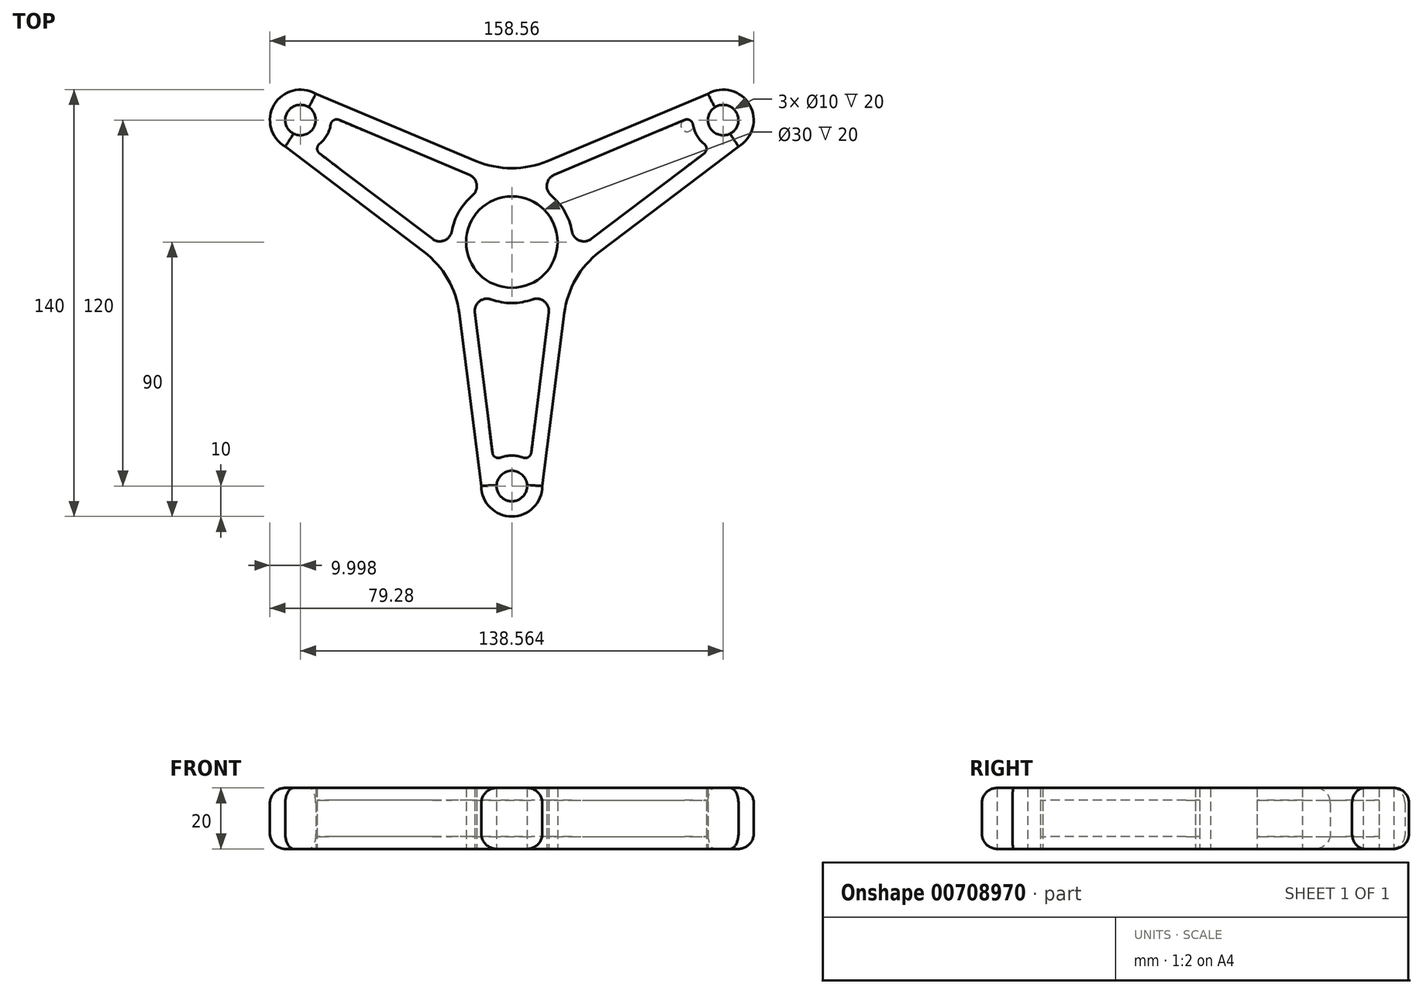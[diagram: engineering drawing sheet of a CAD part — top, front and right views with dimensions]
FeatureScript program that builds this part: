
annotation { "Feature Type Name" : "Feature", "Feature Type Description" : "" }
export const myFeature = defineFeature(function(context is Context, id is Id, definition is map)
    precondition{}
    {
        {
            var Q0;
            Q0=qCreatedBy(makeId("Top.planeOp"),FACE);
            var sketch = newSketch(context, id + "F0", { "sketchPlane" : qUnion([Q0])});
            skCircle(sketch, "E0", {"center": v(0, 0) * mm, "radius": 15 * mm});
            skLineSegment(sketch, "E1", {"start": v(0, 0) * mm, "end": v(-87.42, 50.47) * mm, "construction": true});
            skLineSegment(sketch, "E2", {"start": v(0, 0) * mm, "end": v(80.4, 46.42) * mm, "construction": true});
            skCircle(sketch, "E3", {"center": v(0, -80) * mm, "radius": 5 * mm});
            skLineSegment(sketch, "E4", {"start": v(0, 0) * mm, "end": v(0, -98.48) * mm, "construction": true});
            skArc(sketch, "E5", {"start": v(-10, -80) * mm, "mid": v(0, -90) * mm, "end": v(10, -80) * mm});
            skLineSegment(sketch, "E6", {"start": v(15, 0) * mm, "end": v(14.54, -3.7) * mm});
            skLineSegment(sketch, "E7", {"start": v(-15, 0) * mm, "end": v(-14.54, -3.7) * mm});
            skPoint(sketch, "E8.orphan", {"position": v(-5, -80) * mm});
            skPoint(sketch, "E9.orphan", {"position": v(5, -80) * mm});
            skArc(sketch, "E10.trimOffspring", {"start": v(3.65, -70.7) * mm, "mid": v(0, -70) * mm, "end": v(-3.65, -70.7) * mm});
            skArc(sketch, "E11.filletArc", {"start": v(-6.37, -69.08) * mm, "mid": v(-5.4, -70.55) * mm, "end": v(-3.65, -70.7) * mm});
            skArc(sketch, "E12.filletArc", {"start": v(3.65, -70.7) * mm, "mid": v(5.4, -70.55) * mm, "end": v(6.37, -69.08) * mm});
            skLineSegment(sketch, "E13.trimOffspring", {"start": v(-6.83, -65.35) * mm, "end": v(-6.37, -69.08) * mm});
            skLineSegment(sketch, "E14.trimOffspring", {"start": v(7.68, -58.58) * mm, "end": v(6.37, -69.08) * mm});
            skLineSegment(sketch, "E15", {"start": v(80.4, 46.42) * mm, "end": v(-61.57, -35.55) * mm, "construction": true});
            skLineSegment(sketch, "E16.trimOffspring", {"start": v(-17.2, -23.33) * mm, "end": v(-10, -80) * mm});
            skLineSegment(sketch, "E17", {"start": v(-87.42, 50.47) * mm, "end": v(59.57, -34.4) * mm, "construction": true});
            skLineSegment(sketch, "E18.trimOffspring", {"start": v(17.2, -23.33) * mm, "end": v(10, -80) * mm});
            skCircle(sketch, "E19", {"center": v(-69.28, 40) * mm, "radius": 5 * mm});
            skArc(sketch, "E20", {"start": v(-64.28, 48.66) * mm, "mid": v(-77.94, 45) * mm, "end": v(-74.28, 31.34) * mm});
            skLineSegment(sketch, "E21", {"start": v(-7.5, -13) * mm, "end": v(-10.47, -10.74) * mm});
            skLineSegment(sketch, "E22", {"start": v(7.5, 13) * mm, "end": v(4.07, 14.44) * mm});
            skPoint(sketch, "E23.orphan", {"position": v(-66.78, 44.33) * mm});
            skPoint(sketch, "E24.orphan", {"position": v(-71.78, 35.67) * mm});
            skArc(sketch, "E25.trimOffspring", {"start": v(-63.04, 32.18) * mm, "mid": v(-60.62, 35) * mm, "end": v(-59.4, 38.5) * mm});
            skArc(sketch, "E26.filletArc", {"start": v(-56.64, 40.05) * mm, "mid": v(-58.4, 39.95) * mm, "end": v(-59.4, 38.5) * mm});
            skArc(sketch, "E27.filletArc", {"start": v(-63.04, 32.18) * mm, "mid": v(-63.8, 30.6) * mm, "end": v(-63, 29.03) * mm});
            skLineSegment(sketch, "E28.trimOffspring", {"start": v(-13.92, 22.03) * mm, "end": v(-56.64, 40.05) * mm});
            skLineSegment(sketch, "E29.trimOffspring", {"start": v(-26.04, 1.04) * mm, "end": v(-63, 29.03) * mm});
            skArc(sketch, "E30.trimOffspring", {"start": v(-12.9, 15.29) * mm, "mid": v(-17.32, 10) * mm, "end": v(-19.69, 3.53) * mm});
            skArc(sketch, "E31.filletArc", {"start": v(-12.9, 15.29) * mm, "mid": v(-11.52, 18.94) * mm, "end": v(-13.92, 22.03) * mm});
            skArc(sketch, "E32.filletArc", {"start": v(-26.04, 1.04) * mm, "mid": v(-22.17, 0.5) * mm, "end": v(-19.69, 3.53) * mm});
            skArc(sketch, "E33", {"start": v(-6.79, -18.81) * mm, "mid": v(0, -20) * mm, "end": v(6.79, -18.81) * mm});
            skLineSegment(sketch, "E34.trimOffspring", {"start": v(-11.6, 26.56) * mm, "end": v(-64.28, 48.66) * mm});
            skLineSegment(sketch, "E35.trimOffspring", {"start": v(-28.8, -3.23) * mm, "end": v(-74.28, 31.34) * mm});
            skLineSegment(sketch, "E36.0", {"start": v(-64.28, 48.66) * mm, "end": v(-74.28, 31.34) * mm, "construction": true});
            skArc(sketch, "E37.filletArc", {"start": v(-17.2, -23.33) * mm, "mid": v(-20.98, -12.11) * mm, "end": v(-28.8, -3.23) * mm});
            skLineSegment(sketch, "E38.trimOffspring", {"start": v(-12.12, -23.07) * mm, "end": v(-6.83, -65.35) * mm});
            skLineSegment(sketch, "E39.trimOffspring", {"start": v(12.12, -23.07) * mm, "end": v(6.37, -69.08) * mm});
            skArc(sketch, "E40.trimOffspring", {"start": v(17.32, 10) * mm, "mid": v(15.34, 12.83) * mm, "end": v(12.9, 15.29) * mm});
            skArc(sketch, "E41.filletArc", {"start": v(12.12, -23.07) * mm, "mid": v(10.64, -19.45) * mm, "end": v(6.79, -18.81) * mm});
            skArc(sketch, "E42.filletArc", {"start": v(-6.79, -18.81) * mm, "mid": v(-10.64, -19.45) * mm, "end": v(-12.12, -23.07) * mm});
            skLineSegment(sketch, "E43", {"start": v(0, 0) * mm, "end": v(0, -100.94) * mm, "construction": true});
            skLineSegment(sketch, "E44", {"start": v(0, 0) * mm, "end": v(-80.4, 46.42) * mm, "construction": true});
            skCircle(sketch, "E45", {"center": v(69.28, 40) * mm, "radius": 5 * mm});
            skLineSegment(sketch, "E46", {"start": v(0, 0) * mm, "end": v(85.28, 49.24) * mm, "construction": true});
            skArc(sketch, "E47", {"start": v(74.28, 31.34) * mm, "mid": v(77.94, 45) * mm, "end": v(64.28, 48.66) * mm});
            skLineSegment(sketch, "E48", {"start": v(-7.5, 13) * mm, "end": v(-4.07, 14.44) * mm});
            skLineSegment(sketch, "E49", {"start": v(7.5, -13) * mm, "end": v(10.47, -10.74) * mm});
            skPoint(sketch, "E50.orphan", {"position": v(71.78, 35.67) * mm});
            skPoint(sketch, "E51.orphan", {"position": v(66.78, 44.33) * mm});
            skArc(sketch, "E52.trimOffspring", {"start": v(59.4, 38.5) * mm, "mid": v(60.62, 35) * mm, "end": v(63.04, 32.18) * mm});
            skArc(sketch, "E53.filletArc", {"start": v(63, 29.03) * mm, "mid": v(63.8, 30.6) * mm, "end": v(63.04, 32.18) * mm});
            skArc(sketch, "E54.filletArc", {"start": v(59.4, 38.5) * mm, "mid": v(58.4, 39.95) * mm, "end": v(56.64, 40.05) * mm});
            skLineSegment(sketch, "E55.trimOffspring", {"start": v(26.04, 1.04) * mm, "end": v(63, 29.03) * mm});
            skLineSegment(sketch, "E56.trimOffspring", {"start": v(13.92, 22.03) * mm, "end": v(56.64, 40.05) * mm});
            skArc(sketch, "E57.trimOffspring", {"start": v(19.69, 3.53) * mm, "mid": v(17.32, 10) * mm, "end": v(12.9, 15.29) * mm});
            skArc(sketch, "E58.filletArc", {"start": v(19.69, 3.53) * mm, "mid": v(22.17, 0.5) * mm, "end": v(26.04, 1.04) * mm});
            skArc(sketch, "E59.filletArc", {"start": v(13.92, 22.03) * mm, "mid": v(11.52, 18.94) * mm, "end": v(12.9, 15.29) * mm});
            skLineSegment(sketch, "E60", {"start": v(-80.4, 46.42) * mm, "end": v(61.57, -35.55) * mm, "construction": true});
            skArc(sketch, "E61", {"start": v(-17.32, 10) * mm, "mid": v(-18.78, 6.87) * mm, "end": v(-19.69, 3.53) * mm});
            skLineSegment(sketch, "E62.trimOffspring", {"start": v(28.8, -3.23) * mm, "end": v(74.28, 31.34) * mm});
            skLineSegment(sketch, "E63", {"start": v(0, -100.94) * mm, "end": v(0, 68.79) * mm, "construction": true});
            skLineSegment(sketch, "E64.trimOffspring", {"start": v(11.6, 26.56) * mm, "end": v(64.28, 48.66) * mm});
            skLineSegment(sketch, "E65.0", {"start": v(74.28, 31.34) * mm, "end": v(64.28, 48.66) * mm, "construction": true});
            skArc(sketch, "E66.filletArc", {"start": v(-11.6, 26.56) * mm, "mid": v(0, 24.22) * mm, "end": v(11.6, 26.56) * mm});
            skArc(sketch, "E67.filletArc", {"start": v(28.8, -3.23) * mm, "mid": v(20.98, -12.11) * mm, "end": v(17.2, -23.33) * mm});
            skArc(sketch, "E68.trimOffspring", {"start": v(19.69, 3.53) * mm, "mid": v(18.78, 6.87) * mm, "end": v(17.32, 10) * mm});
            skSolve(sketch);
        }
        {
            var Q0;
            Q0=makeQuery(id+"F0.imprint","IMPRINT",FACE,{"disambiguationData":[TD([[makeQuery(id+"F0.imprint","IMPRINT",EDGE,{"derivedFrom":sQuery(id+"F0.wireOp",EDGE,"E10.trimOffspring")}),-1.0]])]});
            var Q1;
            Q1=makeQuery(id+"F0.imprint","IMPRINT",FACE,{"disambiguationData":[TD([[makeQuery(id+"F0.imprint","IMPRINT",EDGE,{"derivedFrom":sQuery(id+"F0.wireOp",EDGE,"E52.trimOffspring")}),-1.0]])]});
            var Q2;
            Q2=makeQuery(id+"F0.imprint","IMPRINT",FACE,{"disambiguationData":[TD([[makeQuery(id+"F0.imprint","IMPRINT",EDGE,{"derivedFrom":sQuery(id+"F0.wireOp",EDGE,"E25.trimOffspring")}),-1.0]])]});
            extrude(context, id + "F1", {"entities" : qUnion([Q0, Q1, Q2]), "depth" : 12 * mm, "offsetDistance" : 25 * mm, "symmetric" : true});
        }
        {
            var Q0;
            Q0 = qSketchRegion(id + "F0", true);
            extrude(context, id + "F2", {"entities" : qUnion([Q0]), "flatOperationType" : FlatOperationType.REMOVE, "depth" : 20 * mm, "offsetDistance" : 25 * mm, "domain" : OperationDomain.MODEL, "symmetric" : true});
        }
        {
            var Q0;
            Q0=makeQuery(id+"F2.opExtrude","CAP_EDGE",EDGE,{"disambiguationData":[OSD([sQuery(id+"F0.wireOp",EDGE,"E62.trimOffspring")])],"isStart":false});
            var Q1;
            Q1=makeQuery(id+"F2.opExtrude","CAP_EDGE",EDGE,{"disambiguationData":[OSD([sQuery(id+"F0.wireOp",EDGE,"E67.filletArc")])],"isStart":false});
            var Q2;
            Q2=makeQuery(id+"F2.opExtrude","CAP_EDGE",EDGE,{"disambiguationData":[OSD([sQuery(id+"F0.wireOp",EDGE,"E18.trimOffspring")])],"isStart":false});
            var Q3;
            Q3=makeQuery(id+"F2.opExtrude","CAP_EDGE",EDGE,{"disambiguationData":[OSD([sQuery(id+"F0.wireOp",EDGE,"E5")])],"isStart":false});
            var Q4;
            Q4=makeQuery(id+"F2.opExtrude","CAP_EDGE",EDGE,{"disambiguationData":[OSD([sQuery(id+"F0.wireOp",EDGE,"E16.trimOffspring")])],"isStart":false});
            var Q5;
            Q5=makeQuery(id+"F2.opExtrude","CAP_EDGE",EDGE,{"disambiguationData":[OSD([sQuery(id+"F0.wireOp",EDGE,"E20")])],"isStart":false});
            var Q6;
            Q6=makeQuery(id+"F2.opExtrude","CAP_EDGE",EDGE,{"disambiguationData":[OSD([sQuery(id+"F0.wireOp",EDGE,"E35.trimOffspring")])],"isStart":false});
            var Q7;
            Q7=makeQuery(id+"F2.opExtrude","CAP_EDGE",EDGE,{"disambiguationData":[OSD([sQuery(id+"F0.wireOp",EDGE,"E37.filletArc")])],"isStart":false});
            var Q8;
            Q8=makeQuery(id+"F2.opExtrude","CAP_EDGE",EDGE,{"disambiguationData":[OSD([sQuery(id+"F0.wireOp",EDGE,"E34.trimOffspring")])],"isStart":false});
            var Q9;
            Q9=makeQuery(id+"F2.opExtrude","CAP_EDGE",EDGE,{"disambiguationData":[OSD([sQuery(id+"F0.wireOp",EDGE,"E47")])],"isStart":false});
            var Q10;
            Q10=makeQuery(id+"F2.opExtrude","CAP_EDGE",EDGE,{"disambiguationData":[OSD([sQuery(id+"F0.wireOp",EDGE,"E16.trimOffspring")])],"isStart":true});
            var Q11;
            Q11=makeQuery(id+"F2.opExtrude","CAP_EDGE",EDGE,{"disambiguationData":[OSD([sQuery(id+"F0.wireOp",EDGE,"E20")])],"isStart":true});
            var Q12;
            Q12=makeQuery(id+"F2.opExtrude","CAP_EDGE",EDGE,{"disambiguationData":[OSD([sQuery(id+"F0.wireOp",EDGE,"E5")])],"isStart":true});
            var Q13;
            Q13=makeQuery(id+"F2.opExtrude","CAP_EDGE",EDGE,{"disambiguationData":[OSD([sQuery(id+"F0.wireOp",EDGE,"E18.trimOffspring")])],"isStart":true});
            var Q14;
            Q14=makeQuery(id+"F2.opExtrude","CAP_EDGE",EDGE,{"disambiguationData":[OSD([sQuery(id+"F0.wireOp",EDGE,"E67.filletArc")])],"isStart":true});
            var Q15;
            Q15=makeQuery(id+"F2.opExtrude","CAP_EDGE",EDGE,{"disambiguationData":[OSD([sQuery(id+"F0.wireOp",EDGE,"E62.trimOffspring")])],"isStart":true});
            var Q16;
            Q16=makeQuery(id+"F2.opExtrude","CAP_EDGE",EDGE,{"disambiguationData":[OSD([sQuery(id+"F0.wireOp",EDGE,"E47")])],"isStart":true});
            var Q17;
            Q17=makeQuery(id+"F2.opExtrude","CAP_EDGE",EDGE,{"disambiguationData":[OSD([sQuery(id+"F0.wireOp",EDGE,"E64.trimOffspring")])],"isStart":true});
            var Q18;
            Q18=makeQuery(id+"F2.opExtrude","CAP_EDGE",EDGE,{"disambiguationData":[OSD([sQuery(id+"F0.wireOp",EDGE,"E66.filletArc")])],"isStart":true});
            fillet(context, id + "F3", {"entities" : qUnion([Q0, Q1, Q2, Q3, Q4, Q5, Q6, Q7, Q8, Q9, Q10, Q11, Q12, Q13, Q14, Q15, Q16, Q17, Q18]), "radius" : 5 * mm, "tangentPropagation" : true, "allowEdgeOverflow" : false});
        }
    });
